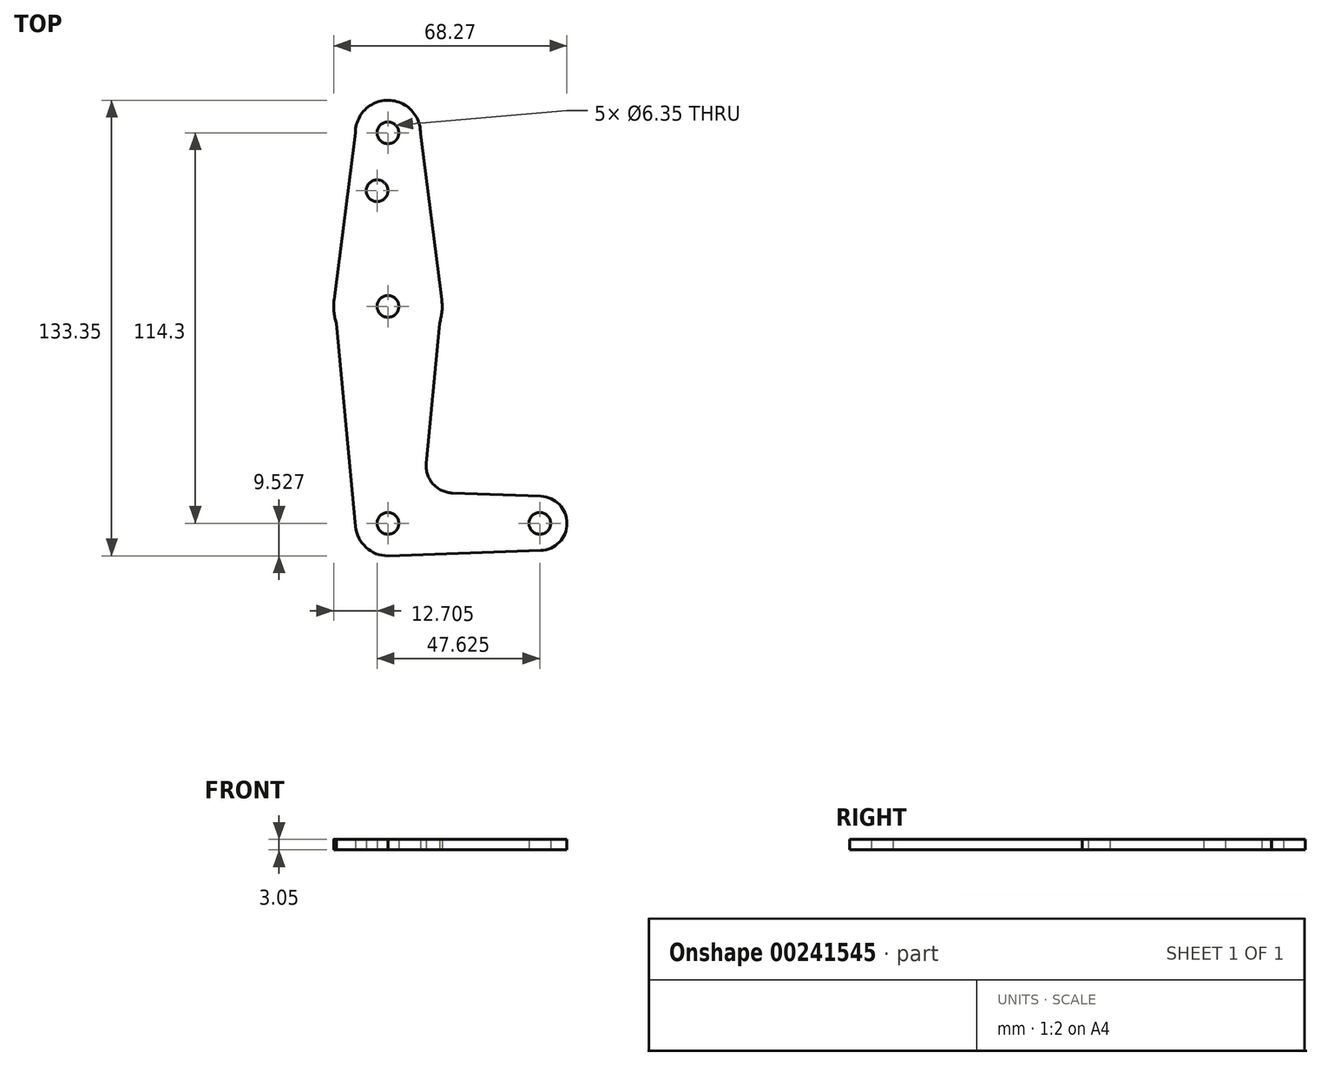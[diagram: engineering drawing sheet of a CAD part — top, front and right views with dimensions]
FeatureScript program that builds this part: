
annotation { "Feature Type Name" : "Feature", "Feature Type Description" : "" }
export const myFeature = defineFeature(function(context is Context, id is Id, definition is map)
    precondition{}
    {
        {
            var Q0;
            Q0=qCreatedBy(makeId("Top.planeOp"),FACE);
            var sketch = newSketch(context, id + "F0", { "sketchPlane" : qUnion([Q0])});
            skCircle(sketch, "E0", {"center": v(0, 76.6) * mm, "radius": 9.53 * mm});
            skCircle(sketch, "E1", {"center": v(0, 25.8) * mm, "radius": 15.88 * mm});
            skCircle(sketch, "E2", {"center": v(0, -37.7) * mm, "radius": 9.53 * mm});
            skCircle(sketch, "E3", {"center": v(44.45, -37.7) * mm, "radius": 7.94 * mm});
            skLineSegment(sketch, "E4", {"start": v(0, -37.7) * mm, "end": v(0, 25.8) * mm});
            skLineSegment(sketch, "E5", {"start": v(0, 25.8) * mm, "end": v(0, 76.6) * mm});
            skLineSegment(sketch, "E6", {"start": v(9.52, 76.28) * mm, "end": v(15.75, 27.82) * mm});
            skLineSegment(sketch, "E7", {"start": v(-9.52, 76.55) * mm, "end": v(-15.75, 27.82) * mm});
            skLineSegment(sketch, "E8", {"start": v(-15.75, 27.82) * mm, "end": v(-9.48, -38.6) * mm});
            skLineSegment(sketch, "E9", {"start": v(15.75, 27.82) * mm, "end": v(11.22, -20.16) * mm});
            skLineSegment(sketch, "E10", {"start": v(0, -47.23) * mm, "end": v(44.73, -45.64) * mm});
            skLineSegment(sketch, "E11", {"start": v(18.85, -28.85) * mm, "end": v(44.73, -29.77) * mm});
            skCircle(sketch, "E12", {"center": v(0, 76.6) * mm, "radius": 3.18 * mm});
            skCircle(sketch, "E13", {"center": v(0, 25.8) * mm, "radius": 3.18 * mm});
            skCircle(sketch, "E14", {"center": v(0, -37.7) * mm, "radius": 3.18 * mm});
            skCircle(sketch, "E15", {"center": v(44.45, -37.7) * mm, "radius": 3.18 * mm});
            skLineSegment(sketch, "E16", {"start": v(-19.93, 27.82) * mm, "end": v(-19.93, 64.35) * mm});
            skLineSegment(sketch, "E17", {"start": v(0, 59.64) * mm, "end": v(-3.17, 59.64) * mm});
            skPoint(sketch, "E18.newPointB", {"position": v(0, -28.18) * mm});
            skArc(sketch, "E18.filletArc", {"start": v(11.22, -20.16) * mm, "mid": v(13.16, -26.15) * mm, "end": v(18.85, -28.85) * mm});
            skCircle(sketch, "E19", {"center": v(-3.17, 59.64) * mm, "radius": 3.18 * mm});
            skSolve(sketch);
        }
        {
            var Q0;
            Q0=makeQuery(id+"F0.imprint","IMPRINT",FACE,{"disambiguationData":[TD([[makeQuery(id+"F0.imprint","IMPRINT",EDGE,{"derivedFrom":sQuery(id+"F0.wireOp",EDGE,"E14")}),-1.0]])]});
            var Q1;
            {var subQ6=sQuery(id+"F0.wireOp",EDGE,"E7");Q1=makeQuery(id+"F0.imprint","IMPRINT",FACE,{"disambiguationData":[TD([[makeQuery(id+"F0.imprint","IMPRINT",EDGE,{"derivedFrom":subQ6}),1.0]])]});}
            var Q2;
            {var subQ1=sQuery(id+"F0.wireOp",EDGE,"E1");var subQ5=sQuery(id+"F0.wireOp",EDGE,"E8");var subQ6=makeQuery(id+"F0.imprint","INTERSECT",VERTEX,{"derivedFrom":[subQ1,subQ5]});Q2=makeQuery(id+"F0.imprint","IMPRINT",FACE,{"disambiguationData":[TD([[makeQuery(id+"F0.imprint","IMPRINT",EDGE,{"disambiguationData":[TD([[subQ6,-1.0]])],"derivedFrom":subQ1}),1.0]])]});}
            var Q3;
            {var subQ1=sQuery(id+"F0.wireOp",EDGE,"E9");var subQ3=sQuery(id+"F0.wireOp",EDGE,"E1");var subQ4=makeQuery(id+"F0.imprint","INTERSECT",VERTEX,{"derivedFrom":[subQ3,subQ1]});Q3=makeQuery(id+"F0.imprint","IMPRINT",FACE,{"disambiguationData":[TD([[makeQuery(id+"F0.imprint","IMPRINT",EDGE,{"disambiguationData":[TD([[subQ4,1.0]])],"derivedFrom":subQ3}),-1.0]])]});}
            var Q4;
            {var subQ2=sQuery(id+"F0.wireOp",EDGE,"E2");var subQ4=sQuery(id+"F0.wireOp",EDGE,"E10");var subQ7=makeQuery(id+"F0.imprint","INTERSECT",VERTEX,{"disambiguationData":[OD(1.0)],"derivedFrom":[subQ2,subQ4]});Q4=makeQuery(id+"F0.imprint","IMPRINT",FACE,{"disambiguationData":[TD([[makeQuery(id+"F0.imprint","IMPRINT",EDGE,{"disambiguationData":[TD([[subQ7,-1.0]])],"derivedFrom":subQ2}),-1.0]])]});}
            var Q5;
            {var subQ4=sQuery(id+"F0.wireOp",EDGE,"E6");Q5=makeQuery(id+"F0.imprint","IMPRINT",FACE,{"disambiguationData":[TD([[makeQuery(id+"F0.imprint","IMPRINT",EDGE,{"derivedFrom":subQ4}),-1.0]])]});}
            var Q6;
            {var subQ0=sQuery(id+"F0.wireOp",EDGE,"E8");var subQ1=sQuery(id+"F0.wireOp",EDGE,"E1");var subQ2=makeQuery(id+"F0.imprint","INTERSECT",VERTEX,{"derivedFrom":[subQ1,subQ0]});Q6=makeQuery(id+"F0.imprint","IMPRINT",FACE,{"disambiguationData":[TD([[makeQuery(id+"F0.imprint","IMPRINT",EDGE,{"disambiguationData":[TD([[subQ2,-1.0]])],"derivedFrom":subQ1}),-1.0]])]});}
            var Q7;
            {var subQ1=sQuery(id+"F0.wireOp",EDGE,"E1");var subQ5=sQuery(id+"F0.wireOp",EDGE,"E9");var subQ7=makeQuery(id+"F0.imprint","INTERSECT",VERTEX,{"derivedFrom":[subQ1,subQ5]});Q7=makeQuery(id+"F0.imprint","IMPRINT",FACE,{"disambiguationData":[TD([[makeQuery(id+"F0.imprint","IMPRINT",EDGE,{"disambiguationData":[TD([[subQ7,1.0]])],"derivedFrom":subQ1}),1.0]])]});}
            var Q8;
            {var subQ0=sQuery(id+"F0.wireOp",EDGE,"E11");var subQ1=sQuery(id+"F0.wireOp",EDGE,"E2");var subQ3=makeQuery(id+"F0.imprint","INTERSECT",VERTEX,{"derivedFrom":[subQ1,subQ0]});Q8=makeQuery(id+"F0.imprint","IMPRINT",FACE,{"disambiguationData":[TD([[makeQuery(id+"F0.imprint","IMPRINT",EDGE,{"disambiguationData":[TD([[subQ3,-1.0]])],"derivedFrom":subQ1}),1.0]])]});}
            var Q9;
            {var subQ0=sQuery(id+"F0.wireOp",EDGE,"E10");var subQ1=sQuery(id+"F0.wireOp",EDGE,"E2");var subQ2=makeQuery(id+"F0.imprint","INTERSECT",VERTEX,{"disambiguationData":[OD(0.0)],"derivedFrom":[subQ1,subQ0]});Q9=makeQuery(id+"F0.imprint","IMPRINT",FACE,{"disambiguationData":[TD([[makeQuery(id+"F0.imprint","IMPRINT",EDGE,{"disambiguationData":[TD([[subQ2,-1.0]])],"derivedFrom":subQ1}),1.0]])]});}
            var Q10;
            {var subQ0=sQuery(id+"F0.wireOp",EDGE,"E8");var subQ1=sQuery(id+"F0.wireOp",EDGE,"E1");var subQ3=makeQuery(id+"F0.imprint","INTERSECT",VERTEX,{"derivedFrom":[subQ1,subQ0]});Q10=makeQuery(id+"F0.imprint","IMPRINT",FACE,{"disambiguationData":[TD([[makeQuery(id+"F0.imprint","IMPRINT",EDGE,{"disambiguationData":[TD([[subQ3,1.0]])],"derivedFrom":subQ1}),1.0]])]});}
            var Q11;
            {var subQ0=sQuery(id+"F0.wireOp",EDGE,"E9");var subQ1=sQuery(id+"F0.wireOp",EDGE,"E1");var subQ3=makeQuery(id+"F0.imprint","INTERSECT",VERTEX,{"derivedFrom":[subQ1,subQ0]});Q11=makeQuery(id+"F0.imprint","IMPRINT",FACE,{"disambiguationData":[TD([[makeQuery(id+"F0.imprint","IMPRINT",EDGE,{"disambiguationData":[TD([[subQ3,-1.0]])],"derivedFrom":subQ1}),1.0]])]});}
            var Q12;
            Q12=makeQuery(id+"F0.imprint","IMPRINT",FACE,{"disambiguationData":[TD([[makeQuery(id+"F0.imprint","IMPRINT",EDGE,{"derivedFrom":sQuery(id+"F0.wireOp",EDGE,"E12")}),-1.0]])]});
            var Q13;
            Q13=makeQuery(id+"F0.imprint","IMPRINT",FACE,{"disambiguationData":[TD([[makeQuery(id+"F0.imprint","IMPRINT",EDGE,{"derivedFrom":sQuery(id+"F0.wireOp",EDGE,"E15")}),-1.0]])]});
            extrude(context, id + "F1", {"entities" : qUnion([Q0, Q1, Q2, Q3, Q4, Q5, Q6, Q7, Q8, Q9, Q10, Q11, Q12, Q13]), "depth" : 3.05 * mm});
        }
    });
